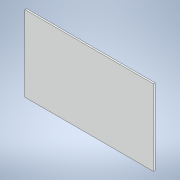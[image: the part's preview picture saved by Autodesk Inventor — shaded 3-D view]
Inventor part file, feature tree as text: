
AUTODESK INVENTOR PART (.ipt)
format: ipt  version: 2021 (Build 250183000, 183)  size: 97,280 bytes
history: native  units: in
note: dims shown in document units (in); Inventor stores cm internally (conversion verified against a paired STEP export)
features: extrude x1, sketch x1
ambient origin geometry x8: Origin, YZ Plane, XZ Plane, XY Plane, X Axis, Y Axis, Z Axis, Center Point
bodies: Solid1 (feature_tree)
feature tree (2):
  extrude  "Extrusion1"  Depth=1.7717in
  sketch  "Sketch1"  dims[d0=3.0in d1=1.7717in d2=0.0394in d3=0.0in]
